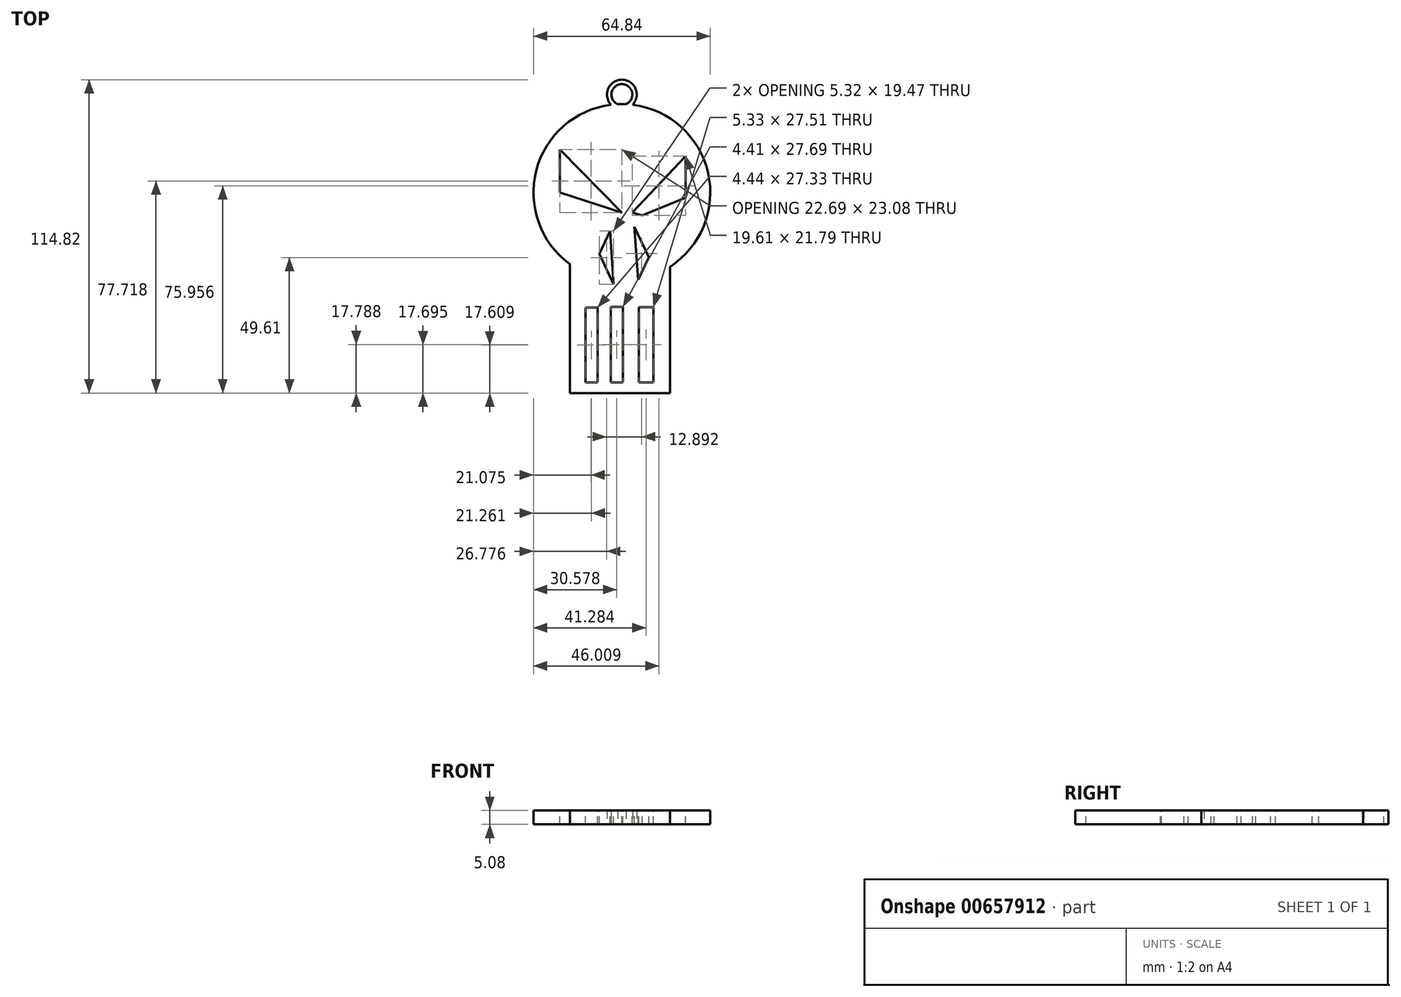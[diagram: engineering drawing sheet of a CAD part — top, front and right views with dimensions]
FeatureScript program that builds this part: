
annotation { "Feature Type Name" : "Feature", "Feature Type Description" : "" }
export const myFeature = defineFeature(function(context is Context, id is Id, definition is map)
    precondition{}
    {
        {
            var Q0;
            Q0=qCreatedBy(makeId("Top.planeOp"),FACE);
            var sketch = newSketch(context, id + "F0", { "sketchPlane" : qUnion([Q0])});
            skCircle(sketch, "E0", {"center": v(0, 0) * mm, "radius": 5.45 * mm});
            skSolve(sketch);
        }
        {
            var Q0;
            Q0 = qSketchRegion(id + "F0", true);
            extrude(context, id + "F1", {"entities" : qUnion([Q0]), "depth" : 5.08 * mm, "offsetDistance" : 25.4 * mm});
        }
        {
            var Q0;
            Q0=makeQuery(id+"F1.opExtrude","CAP_FACE",FACE,{"disambiguationData":[OSD([sQuery(id+"F0.wireOp",EDGE,"E0")])],"isStart":false});
            var sketch = newSketch(context, id + "F2", { "sketchPlane" : qUnion([Q0])});
            skCircle(sketch, "E1", {"center": v(0, 0) * mm, "radius": 3.83 * mm});
            skSolve(sketch);
        }
        {
            var Q0;
            Q0 = qSketchRegion(id + "F2", true);
            extrude(context, id + "F3", {"entities" : qUnion([Q0]), "operationType" : NewBodyOperationType.REMOVE, "oppositeDirection" : true, "depth" : 25.4 * mm, "offsetDistance" : 25.4 * mm});
        }
        {
            var Q0;
            Q0=qCreatedBy(makeId("Top.planeOp"),FACE);
            var sketch = newSketch(context, id + "F4", { "sketchPlane" : qUnion([Q0])});
            skCircle(sketch, "E2", {"center": v(0, -35.92) * mm, "radius": 32.42 * mm});
            skSolve(sketch);
        }
        {
            var Q0;
            Q0 = qSketchRegion(id + "F4", true);
            extrude(context, id + "F5", {"entities" : qUnion([Q0]), "operationType" : NewBodyOperationType.ADD, "depth" : 5.08 * mm, "offsetDistance" : 25.4 * mm});
        }
        {
            var Q0;
            Q0=qCreatedBy(makeId("Top.planeOp"),FACE);
            var sketch = newSketch(context, id + "F6", { "sketchPlane" : qUnion([Q0])});
            skLineSegment(sketch, "E3.bottom", {"start": v(-19.1, -44.07) * mm, "end": v(17.62, -44.07) * mm});
            skLineSegment(sketch, "E3.top", {"start": v(-19.1, -109.37) * mm, "end": v(17.62, -109.37) * mm});
            skLineSegment(sketch, "E3.left", {"start": v(-19.1, -44.07) * mm, "end": v(-19.1, -109.37) * mm});
            skLineSegment(sketch, "E3.right", {"start": v(17.62, -44.07) * mm, "end": v(17.62, -109.37) * mm});
            skSolve(sketch);
        }
        {
            var Q0;
            Q0 = qSketchRegion(id + "F6", true);
            extrude(context, id + "F7", {"entities" : qUnion([Q0]), "operationType" : NewBodyOperationType.ADD, "depth" : 5.08 * mm, "offsetDistance" : 25.4 * mm});
        }
        {
            var Q0;
            Q0=makeQuery(id+"F7.boolean.opBoolean","MERGE",FACE,{"derivedFrom":[makeQuery(id+"F5.boolean.opBoolean","MERGE",FACE,{"derivedFrom":[makeQuery(id+"F1.opExtrude","CAP_FACE",FACE,{"disambiguationData":[OSD([sQuery(id+"F0.wireOp",EDGE,"E0")])],"isStart":false}),makeQuery(id+"F5.opExtrude","CAP_FACE",FACE,{"disambiguationData":[OSD([sQuery(id+"F4.wireOp",EDGE,"E2")])],"isStart":false})]}),makeQuery(id+"F7.opExtrude","CAP_FACE",FACE,{"disambiguationData":[OSD([sQuery(id+"F6.wireOp",EDGE,"E3.bottom"),sQuery(id+"F6.wireOp",EDGE,"E3.top"),sQuery(id+"F6.wireOp",EDGE,"E3.left"),sQuery(id+"F6.wireOp",EDGE,"E3.right")])],"isStart":false})]});
            var sketch = newSketch(context, id + "F8", { "sketchPlane" : qUnion([Q0])});
            skSolve(sketch);
        }
        {
            var Q0;
            {var subQ1=sQuery(id+"F0.wireOp",EDGE,"E0");Q0=makeQuery(id+"F8.imprint","IMPRINT",FACE,{"disambiguationData":[TD([[makeQuery(id+"F8.imprint","IMPRINT",EDGE,{"derivedFrom":makeQuery(id+"F1.opExtrude","CAP_EDGE",EDGE,{"disambiguationData":[OSD([subQ1])],"isStart":false})}),1.0]])]});}
            var sketch = newSketch(context, id + "F9", { "sketchPlane" : qUnion([Q0])});
            skLineSegment(sketch, "E4.bottom", {"start": v(-13.38, -105.43) * mm, "end": v(-8.94, -105.43) * mm});
            skLineSegment(sketch, "E4.top", {"start": v(-13.38, -78.1) * mm, "end": v(-8.94, -78.1) * mm});
            skLineSegment(sketch, "E4.left", {"start": v(-13.38, -105.43) * mm, "end": v(-13.38, -78.1) * mm});
            skLineSegment(sketch, "E4.right", {"start": v(-8.94, -105.43) * mm, "end": v(-8.94, -78.1) * mm});
            skLineSegment(sketch, "E5.bottom", {"start": v(-4.05, -105.43) * mm, "end": v(0.36, -105.43) * mm});
            skLineSegment(sketch, "E5.top", {"start": v(-4.05, -77.74) * mm, "end": v(0.36, -77.74) * mm});
            skLineSegment(sketch, "E5.left", {"start": v(-4.05, -105.43) * mm, "end": v(-4.05, -77.74) * mm});
            skLineSegment(sketch, "E5.right", {"start": v(0.36, -105.43) * mm, "end": v(0.36, -77.74) * mm});
            skLineSegment(sketch, "E6.bottom", {"start": v(6.2, -105.43) * mm, "end": v(11.53, -105.43) * mm});
            skLineSegment(sketch, "E6.top", {"start": v(6.2, -77.92) * mm, "end": v(11.53, -77.92) * mm});
            skLineSegment(sketch, "E6.left", {"start": v(6.2, -105.43) * mm, "end": v(6.2, -77.92) * mm});
            skLineSegment(sketch, "E6.right", {"start": v(11.53, -105.43) * mm, "end": v(11.53, -77.92) * mm});
            skSolve(sketch);
        }
        {
            var Q0;
            Q0 = qSketchRegion(id + "F9", true);
            extrude(context, id + "F10", {"entities" : qUnion([Q0]), "operationType" : NewBodyOperationType.REMOVE, "oppositeDirection" : true, "depth" : 25.4 * mm, "offsetDistance" : 25.4 * mm});
        }
        {
            var Q0;
            {var subQ1=sQuery(id+"F0.wireOp",EDGE,"E0");Q0=makeQuery(id+"F8.imprint","IMPRINT",FACE,{"disambiguationData":[TD([[makeQuery(id+"F8.imprint","IMPRINT",EDGE,{"derivedFrom":makeQuery(id+"F1.opExtrude","CAP_EDGE",EDGE,{"disambiguationData":[OSD([subQ1])],"isStart":false})}),1.0]])]});}
            var sketch = newSketch(context, id + "F11", { "sketchPlane" : qUnion([Q0])});
            skLineSegment(sketch, "E7", {"start": v(4.59, -48.46) * mm, "end": v(9.9, -59.6) * mm});
            skLineSegment(sketch, "E8", {"start": v(9.9, -59.6) * mm, "end": v(5.98, -67.93) * mm});
            skLineSegment(sketch, "E9", {"start": v(5.98, -67.93) * mm, "end": v(4.59, -48.46) * mm});
            skLineSegment(sketch, "E10", {"start": v(-2.98, -69.5) * mm, "end": v(-8.3, -58.36) * mm});
            skLineSegment(sketch, "E11", {"start": v(-8.3, -58.36) * mm, "end": v(-4.37, -50.02) * mm});
            skLineSegment(sketch, "E12", {"start": v(-4.37, -50.02) * mm, "end": v(-2.98, -69.5) * mm});
            skSolve(sketch);
        }
        {
            var Q0;
            Q0 = qSketchRegion(id + "F11", true);
            extrude(context, id + "F12", {"entities" : qUnion([Q0]), "operationType" : NewBodyOperationType.REMOVE, "oppositeDirection" : true, "depth" : 25.4 * mm, "offsetDistance" : 25.4 * mm});
        }
        {
            var Q0;
            {var subQ1=sQuery(id+"F0.wireOp",EDGE,"E0");Q0=makeQuery(id+"F8.imprint","IMPRINT",FACE,{"disambiguationData":[TD([[makeQuery(id+"F8.imprint","IMPRINT",EDGE,{"derivedFrom":makeQuery(id+"F1.opExtrude","CAP_EDGE",EDGE,{"disambiguationData":[OSD([subQ1])],"isStart":false})}),1.0]])]});}
            var sketch = newSketch(context, id + "F13", { "sketchPlane" : qUnion([Q0])});
            skLineSegment(sketch, "E13", {"start": v(3.78, -43.2) * mm, "end": v(23.4, -22.52) * mm});
            skLineSegment(sketch, "E14", {"start": v(23.4, -22.52) * mm, "end": v(23.4, -37.76) * mm});
            skLineSegment(sketch, "E15", {"start": v(23.4, -37.76) * mm, "end": v(7.48, -44.3) * mm});
            skLineSegment(sketch, "E16", {"start": v(7.48, -44.3) * mm, "end": v(3.78, -43.2) * mm});
            skLineSegment(sketch, "E17", {"start": v(-22.7, -20.11) * mm, "end": v(0, -43.2) * mm});
            skLineSegment(sketch, "E18", {"start": v(-22.7, -20.11) * mm, "end": v(-22.7, -35.92) * mm});
            skLineSegment(sketch, "E19", {"start": v(-22.7, -35.92) * mm, "end": v(0, -43.2) * mm});
            skSolve(sketch);
        }
        {
            var Q0;
            Q0 = qSketchRegion(id + "F13", true);
            extrude(context, id + "F14", {"entities" : qUnion([Q0]), "operationType" : NewBodyOperationType.REMOVE, "oppositeDirection" : true, "depth" : 25.4 * mm, "offsetDistance" : 25.4 * mm});
        }
    });
